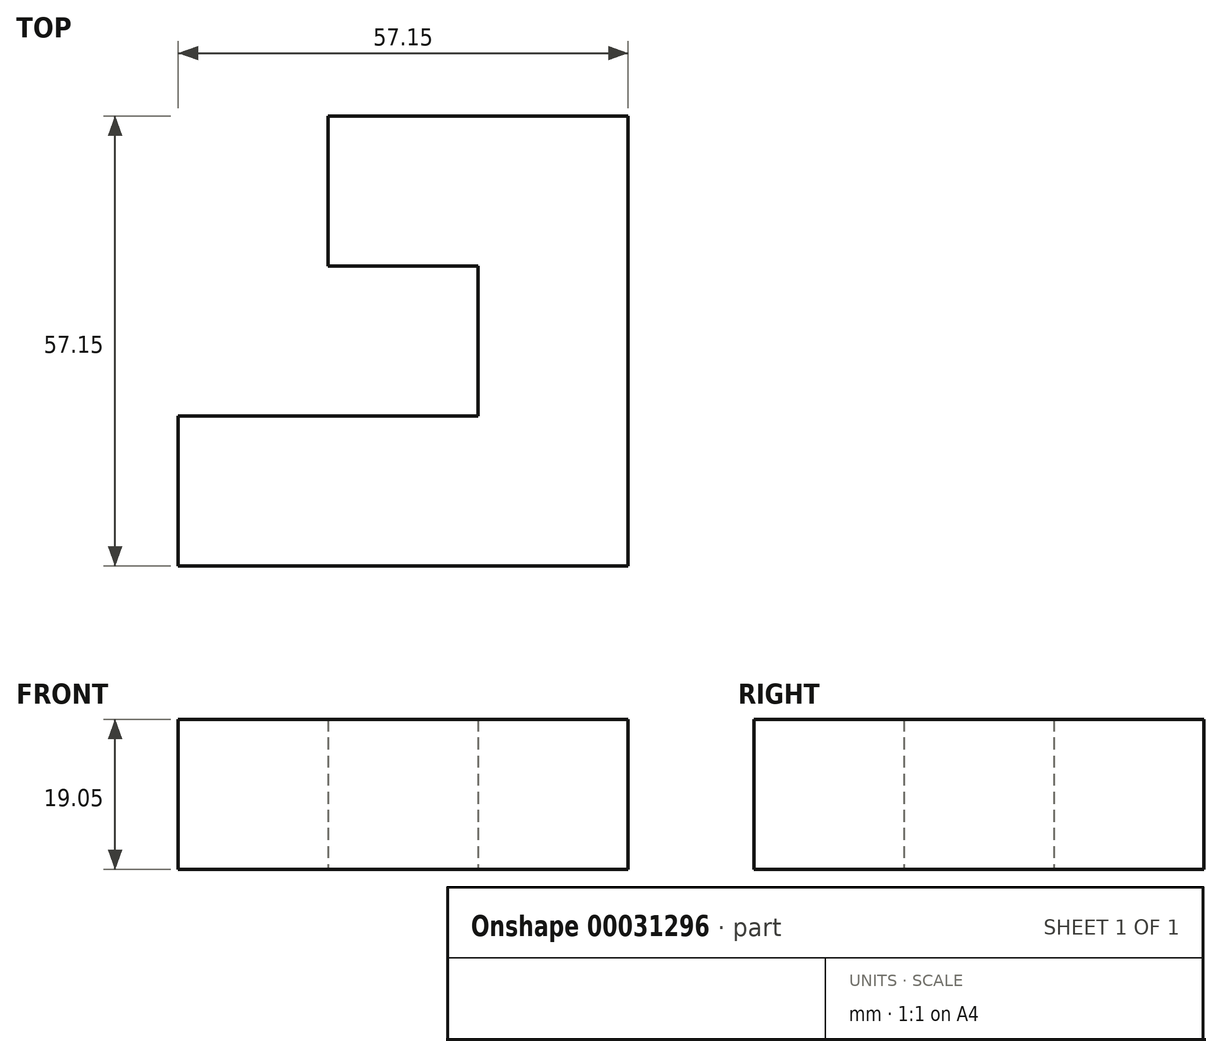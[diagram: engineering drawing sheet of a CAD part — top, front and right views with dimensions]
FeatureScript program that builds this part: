
annotation { "Feature Type Name" : "Feature", "Feature Type Description" : "" }
export const myFeature = defineFeature(function(context is Context, id is Id, definition is map)
    precondition{}
    {
        {
            var Q0;
            Q0=qCreatedBy(makeId("Top.planeOp"),FACE);
            var sketch = newSketch(context, id + "F0", { "sketchPlane" : qUnion([Q0])});
            skLineSegment(sketch, "E0", {"start": v(0, 0) * mm, "end": v(57.15, 0) * mm});
            skLineSegment(sketch, "E1", {"start": v(57.15, 0) * mm, "end": v(57.15, 57.15) * mm});
            skLineSegment(sketch, "E2", {"start": v(57.15, 57.15) * mm, "end": v(19.05, 57.15) * mm});
            skLineSegment(sketch, "E3", {"start": v(19.05, 57.15) * mm, "end": v(19.05, 38.1) * mm});
            skLineSegment(sketch, "E4", {"start": v(19.05, 38.1) * mm, "end": v(38.1, 38.1) * mm});
            skLineSegment(sketch, "E5", {"start": v(38.1, 38.1) * mm, "end": v(38.1, 19.05) * mm});
            skLineSegment(sketch, "E6", {"start": v(38.1, 19.05) * mm, "end": v(0, 19.05) * mm});
            skLineSegment(sketch, "E7", {"start": v(0, 19.05) * mm, "end": v(0, 0) * mm});
            skSolve(sketch);
        }
        {
            var Q0;
            Q0=makeQuery(id+"F0.imprint","IMPRINT",FACE,{"disambiguationData":[TD([[makeQuery(id+"F0.imprint","IMPRINT",EDGE,{"derivedFrom":sQuery(id+"F0.wireOp",EDGE,"E0")}),1.0]])]});
            extrude(context, id + "F1", {"entities" : qUnion([Q0]), "depth" : 19.05 * mm});
        }
    });
